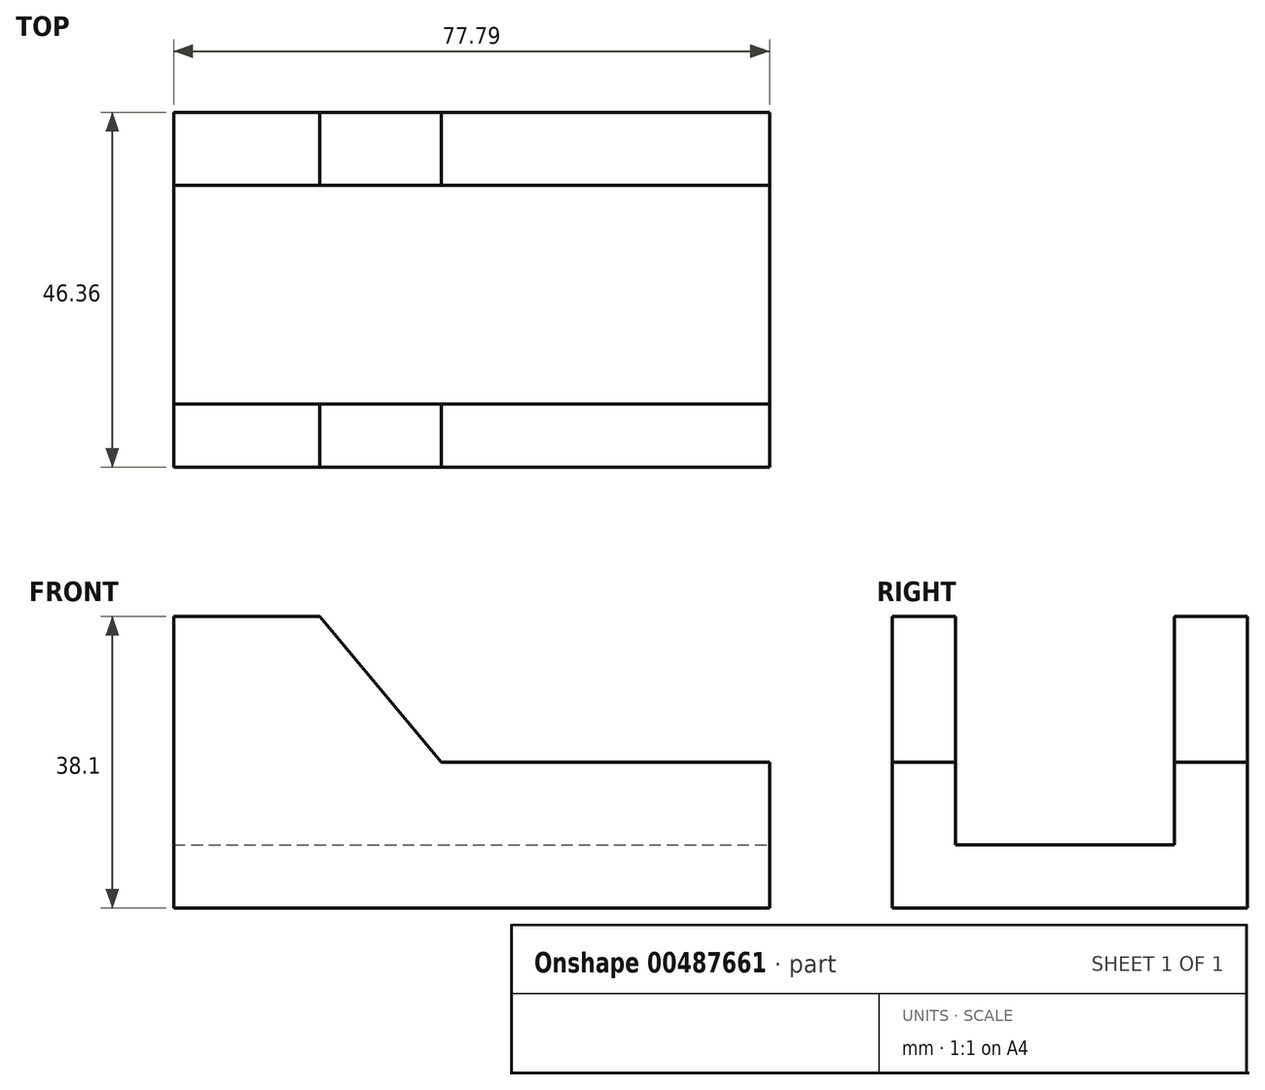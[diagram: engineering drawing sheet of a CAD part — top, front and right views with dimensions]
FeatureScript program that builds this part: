
annotation { "Feature Type Name" : "Feature", "Feature Type Description" : "" }
export const myFeature = defineFeature(function(context is Context, id is Id, definition is map)
    precondition{}
    {
        {
            var Q0;
            Q0=qCreatedBy(makeId("Front.planeOp"),FACE);
            var sketch = newSketch(context, id + "F0", { "sketchPlane" : qUnion([Q0])});
            skLineSegment(sketch, "E0", {"start": v(-0.69, 24.16) * mm, "end": v(-0.69, -13.94) * mm});
            skLineSegment(sketch, "E1", {"start": v(-0.69, -13.94) * mm, "end": v(77.1, -13.94) * mm});
            skLineSegment(sketch, "E2", {"start": v(77.1, -13.94) * mm, "end": v(77.1, 5.11) * mm});
            skLineSegment(sketch, "E3", {"start": v(77.1, 5.11) * mm, "end": v(34.24, 5.11) * mm});
            skLineSegment(sketch, "E4", {"start": v(34.24, 5.11) * mm, "end": v(18.36, 24.16) * mm});
            skLineSegment(sketch, "E5", {"start": v(18.36, 24.16) * mm, "end": v(-0.69, 24.16) * mm});
            skLineSegment(sketch, "E6", {"start": v(-0.69, -5.68) * mm, "end": v(77.1, -5.68) * mm});
            skSolve(sketch);
        }
        {
            var Q0;
            Q0=qSketchRegion(id+"F0",true);
            extrude(context, id + "F1", {"entities" : qUnion([Q0]), "depth" : 8.25 * mm});
        }
        {
            var Q0;
            {var subQ0=sQuery(id+"F0.wireOp",EDGE,"E1");Q0=makeQuery(id+"F0.imprint","IMPRINT",FACE,{"disambiguationData":[TD([[makeQuery(id+"F0.imprint","IMPRINT",EDGE,{"derivedFrom":subQ0}),1.0]])]});}
            extrude(context, id + "F2", {"entities" : qUnion([Q0]), "operationType" : NewBodyOperationType.ADD, "oppositeDirection" : true, "depth" : 28.57 * mm});
        }
        {
            var Q0;
            Q0=makeQuery(id+"F2.opExtrude","CAP_FACE",FACE,{"disambiguationData":[OSD([sQuery(id+"F0.wireOp",EDGE,"E0"),sQuery(id+"F0.wireOp",EDGE,"E1"),sQuery(id+"F0.wireOp",EDGE,"E2"),sQuery(id+"F0.wireOp",EDGE,"E6")])],"isStart":false});
            var sketch = newSketch(context, id + "F3", { "sketchPlane" : qUnion([Q0])});
            skLineSegment(sketch, "E7", {"start": v(-77.1, -13.94) * mm, "end": v(-77.1, 5.11) * mm});
            skLineSegment(sketch, "E8", {"start": v(-77.1, 5.11) * mm, "end": v(-34.24, 5.11) * mm});
            skLineSegment(sketch, "E9", {"start": v(-34.24, 5.11) * mm, "end": v(-18.36, 24.16) * mm});
            skLineSegment(sketch, "E10", {"start": v(-18.36, 24.16) * mm, "end": v(0.69, 24.16) * mm});
            skLineSegment(sketch, "E11", {"start": v(0.69, 24.16) * mm, "end": v(0.69, -13.94) * mm});
            skLineSegment(sketch, "E12", {"start": v(0.69, -13.94) * mm, "end": v(-77.1, -13.94) * mm});
            skSolve(sketch);
        }
        {
            var Q0;
            {var subQ0=sQuery(id+"F3.wireOp",EDGE,"E12");Q0=makeQuery(id+"F3.imprint","IMPRINT",FACE,{"disambiguationData":[TD([[makeQuery(id+"F3.imprint","IMPRINT",EDGE,{"derivedFrom":subQ0}),-1.0]])]});}
            var Q1;
            {var subQ1=sQuery(id+"F3.wireOp",EDGE,"E8");Q1=makeQuery(id+"F3.imprint","IMPRINT",FACE,{"disambiguationData":[TD([[makeQuery(id+"F3.imprint","IMPRINT",EDGE,{"derivedFrom":subQ1}),-1.0]])]});}
            extrude(context, id + "F4", {"entities" : qUnion([Q0, Q1]), "operationType" : NewBodyOperationType.ADD, "depth" : 9.52 * mm});
        }
    });
